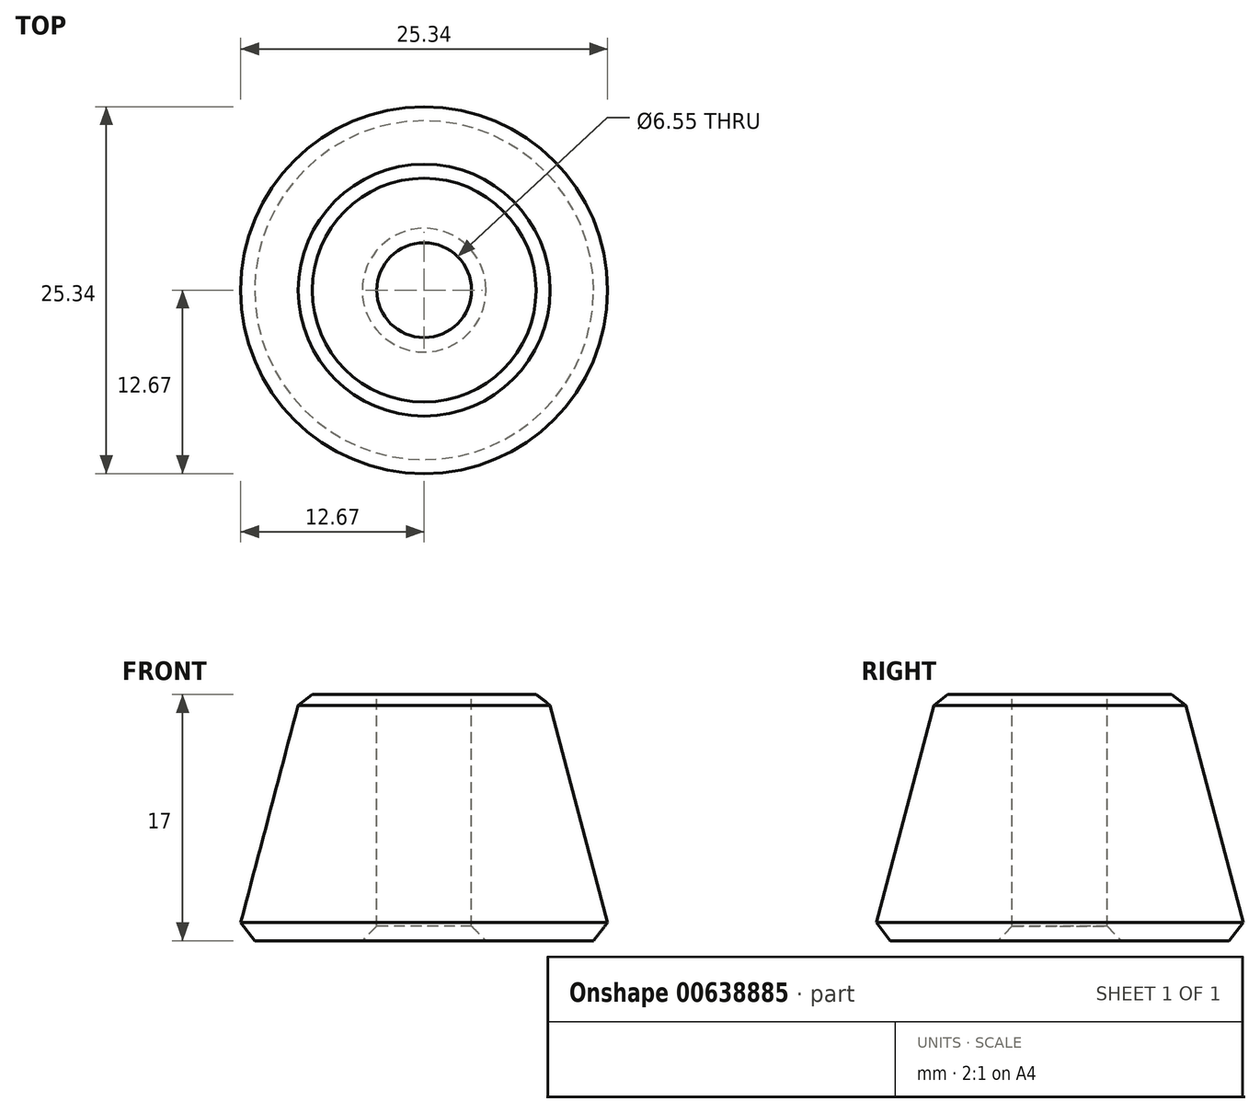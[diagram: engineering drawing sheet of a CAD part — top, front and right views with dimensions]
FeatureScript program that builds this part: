
annotation { "Feature Type Name" : "Feature", "Feature Type Description" : "" }
export const myFeature = defineFeature(function(context is Context, id is Id, definition is map)
    precondition{}
    {
        {
            var Q0;
            Q0=qCreatedBy(makeId("Top.planeOp"),FACE);
            var sketch = newSketch(context, id + "F0", { "sketchPlane" : qUnion([Q0])});
            skCircle(sketch, "E0", {"center": v(0, 0) * mm, "radius": 13 * mm});
            skCircle(sketch, "E1", {"center": v(0, 0) * mm, "radius": 3.2 * mm, "construction": true});
            skSolve(sketch);
        }
        {
            var Q0;
            Q0=makeQuery(id+"F0.imprint","IMPRINT",FACE,{"disambiguationData":[TD([[makeQuery(id+"F0.imprint","IMPRINT",EDGE,{"derivedFrom":sQuery(id+"F0.wireOp",EDGE,"E0")}),1.0]])]});
            cPlane(context, id + "F1", {"entities" : qUnion([Q0]), "cplaneType" : CPlaneType.OFFSET, "offset" : 17 * mm, "width" : 150 * mm, "height" : 150 * mm});
        }
        {
            var Q0;
            Q0=qCreatedBy(id+"F1.planeOp",FACE);
            var sketch = newSketch(context, id + "F2", { "sketchPlane" : qUnion([Q0])});
            skCircle(sketch, "E2", {"center": v(0, 0) * mm, "radius": 8.5 * mm});
            skSolve(sketch);
        }
        {
            var Q0;
            Q0=makeQuery(id+"F0.imprint","IMPRINT",FACE,{"disambiguationData":[TD([[makeQuery(id+"F0.imprint","IMPRINT",EDGE,{"derivedFrom":sQuery(id+"F0.wireOp",EDGE,"E0")}),1.0]])]});
            var Q1;
            Q1=makeQuery(id+"F2.imprint","IMPRINT",FACE,{"disambiguationData":[TD([[makeQuery(id+"F2.imprint","IMPRINT",EDGE,{"derivedFrom":sQuery(id+"F2.wireOp",EDGE,"E2")}),1.0]])]});
            loft(context, id + "F3", {"sheetProfilesArray" : [{ "sheetProfileEntities" : qUnion([Q0]) }, { "sheetProfileEntities" : qUnion([Q1]) }]});
        }
        {
            var Q0;
            Q0=makeQuery(id+"F2.imprint","IMPRINT",FACE,{"disambiguationData":[TD([[makeQuery(id+"F2.imprint","IMPRINT",EDGE,{"derivedFrom":sQuery(id+"F2.wireOp",EDGE,"E2")}),1.0]])]});
            var sketch = newSketch(context, id + "F4", { "sketchPlane" : qUnion([Q0])});
            skCircle(sketch, "E3", {"center": v(0, 0) * mm, "radius": 3.28 * mm});
            skSolve(sketch);
        }
        {
            var Q0;
            Q0=makeQuery(id+"F4.imprint","IMPRINT",FACE,{"disambiguationData":[TD([[makeQuery(id+"F4.imprint","IMPRINT",EDGE,{"derivedFrom":sQuery(id+"F4.wireOp",EDGE,"E3")}),1.0]])]});
            extrude(context, id + "F5", {"entities" : qUnion([Q0]), "operationType" : NewBodyOperationType.REMOVE, "oppositeDirection" : true, "depth" : 25 * mm, "offsetDistance" : 25 * mm});
        }
        {
            var Q0;
            Q0=makeQuery(id+"F5.boolean.opBoolean","COPY",EDGE,{"derivedFrom":makeQuery(id+"F5.opExtrude","CAP_EDGE",EDGE,{"disambiguationData":[OSD([sQuery(id+"F4.wireOp",EDGE,"E3")])],"isStart":true})});
            var Q1;
            Q1=makeQuery(id+"F3.opLoft","MID_CAP_EDGE",EDGE,{"disambiguationData":[OSD([sQuery(id+"F2.wireOp",EDGE,"E2")])],"capPos":1.0});
            var Q2;
            Q2=makeQuery(id+"F3.opLoft","MID_CAP_EDGE",EDGE,{"disambiguationData":[OSD([sQuery(id+"F0.wireOp",EDGE,"E0")])],"capPos":0.0});
            var Q3;
            Q3=makeQuery(id+"F5.boolean.opBoolean","INTERSECT",EDGE,{"derivedFrom":[makeQuery(id+"F3.opLoft","CAP_FACE",FACE,{"disambiguationData":[OSD([makeQuery(id+"F0.imprint","IMPRINT",FACE,{"disambiguationData":[TD([[makeQuery(id+"F0.imprint","IMPRINT",EDGE,{"derivedFrom":sQuery(id+"F0.wireOp",EDGE,"E0")}),1.0]])]})])],"isStart":true}),makeQuery(id+"F5.opExtrude","SWEPT_FACE",FACE,{"disambiguationData":[OSD([sQuery(id+"F4.wireOp",EDGE,"E3")])]})]});
            chamfer(context, id + "F6", {"entities" : qUnion([Q0, Q1, Q2, Q3]), "width" : 1 * mm, "tangentPropagation" : true});
        }
    });
